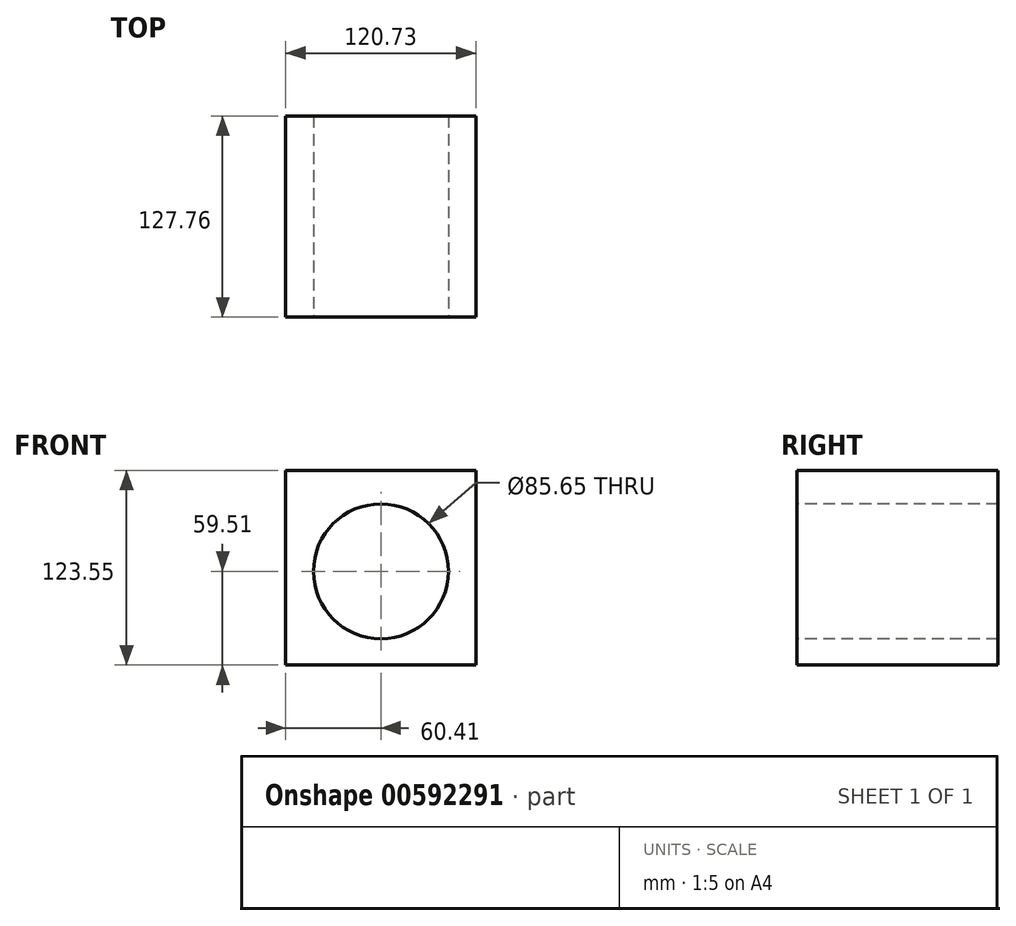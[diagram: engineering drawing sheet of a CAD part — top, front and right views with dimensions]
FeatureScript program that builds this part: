
annotation { "Feature Type Name" : "Feature", "Feature Type Description" : "" }
export const myFeature = defineFeature(function(context is Context, id is Id, definition is map)
    precondition{}
    {
        {
            var Q0;
            Q0=qCreatedBy(makeId("Top.planeOp"),FACE);
            var sketch = newSketch(context, id + "F0", { "sketchPlane" : qUnion([Q0])});
            skLineSegment(sketch, "E0.bottom", {"start": v(44.91, -46.43) * mm, "end": v(-44.91, -46.43) * mm});
            skLineSegment(sketch, "E0.top", {"start": v(44.91, 46.43) * mm, "end": v(-44.91, 46.43) * mm});
            skLineSegment(sketch, "E0.left", {"start": v(44.91, -46.43) * mm, "end": v(44.91, 46.43) * mm});
            skLineSegment(sketch, "E0.right", {"start": v(-44.91, -46.43) * mm, "end": v(-44.91, 46.43) * mm});
            skPoint(sketch, "E0.middle", {"position": v(0, 0) * mm});
            skLineSegment(sketch, "E1.bottom", {"start": v(82.33, -65.12) * mm, "end": v(7.5, -65.12) * mm});
            skLineSegment(sketch, "E1.top", {"start": v(82.33, -27.75) * mm, "end": v(7.5, -27.75) * mm});
            skLineSegment(sketch, "E1.left", {"start": v(82.33, -65.12) * mm, "end": v(82.33, -27.75) * mm});
            skLineSegment(sketch, "E1.right", {"start": v(7.5, -65.12) * mm, "end": v(7.5, -27.75) * mm});
            skPoint(sketch, "E1.middle", {"position": v(44.91, -46.43) * mm});
            skSolve(sketch);
        }
        {
            var Q0;
            Q0=qCreatedBy(makeId("Front.planeOp"),FACE);
            var sketch = newSketch(context, id + "F1", { "sketchPlane" : qUnion([Q0])});
            skLineSegment(sketch, "E2.bottom", {"start": v(-60.4, -59.51) * mm, "end": v(60.32, -59.51) * mm});
            skLineSegment(sketch, "E2.top", {"start": v(-60.4, 64.04) * mm, "end": v(60.32, 64.04) * mm});
            skLineSegment(sketch, "E2.left", {"start": v(-60.4, -59.51) * mm, "end": v(-60.4, 64.04) * mm});
            skLineSegment(sketch, "E2.right", {"start": v(60.32, -59.51) * mm, "end": v(60.32, 64.04) * mm});
            skCircle(sketch, "E3", {"center": v(0, 0) * mm, "radius": 42.82 * mm});
            skLineSegment(sketch, "E4.0", {"start": v(44.91, 0) * mm, "end": v(-44.91, 0) * mm});
            skLineSegment(sketch, "E4.1", {"start": v(44.91, 0) * mm, "end": v(-44.91, 0) * mm});
            skSolve(sketch);
        }
        {
            var Q0;
            Q0 = qSketchRegion(id + "F1", true);
            extrude(context, id + "F2", {"entities" : qUnion([Q0]), "oppositeDirection" : true, "depth" : 127.76 * mm, "offsetDistance" : 25.4 * mm});
        }
    });
